# Revit family: Haworth_9_OccasionalTable
name_source: partatom
category: Furniture
revit_build: Autodesk Revit 2018 (Build: 20170223_1515(x64)
units: mm (PartAtom-declared; Revit-internal decimal feet)

## family parameters
Always vertical = Yes
Cut with Voids When Loaded = No
OmniClass Number = 23.40.70.14.64.21
OmniClass Title = Systems Furniture
Room Calculation Point = No
Shared = No
Work Plane-Based = No

## types (10) — shared parameters
Assembly Code = E2020200
Description = Haworth - Cassina - 9 - Occasional Table
Manufacturer = Haworth
Model = Haworth - Cassina - 9
Revision Number = 1
Size = Verify Final Dim. w/ Haworth
Sustainability Info = https://www.haworth.com
URL = https://www.haworth.com
URL - Product = https://www.haworth.com
Warranty = http://www.haworth.com

## per-type parameters (varying)
| type | Actual Depth | Actual Diameter | Actual Height | Bottom Base | Glass Top | Height Diff for Stone Top | High | Large | Low | Medium | Small | Wood or Stone Top |
| Low Occasional Table -  Glass Top With Stone Base | 15.7 " | 15.7 " | 17.7 " | 3.92 " | Yes | 0 " | No | No | Yes | No | Yes | No |
| Medium Occasional Table -  Glass Top With Stone Base | 15.7 " | 15.7 " | 19.7 " | 3.92 " | Yes | 0 " | No | No | No | Yes | Yes | No |
| High Occasional Table -  Glass Top With Stone Base | 15.7 " | 15.7 " | 21.7 " | 3.92 " | Yes | 0 " | Yes | No | No | No | Yes | No |
| Low Occasional Table -  Wood Top And Base | 15.7 " | 15.7 " | 17.3 " | 3.92 " | No | 0.4 " | No | No | Yes | No | Yes | Yes |
| Medium Occasional Table -  Wood Top And Base | 15.7 " | 15.7 " | 19.3 " | 3.92 " | No | 0.4 " | No | No | No | Yes | Yes | Yes |
| High Occasional Table -  Wood Top And Base | 15.7 " | 15.7 " | 21.3 " | 3.92 " | No | 0.4 " | Yes | No | No | No | Yes | Yes |
| Low Occasional Table -  Stone Top And Base | 15.7 " | 15.7 " | 17.3 " | 3.92 " | No | 0.4 " | No | No | Yes | No | Yes | Yes |
| Medium Occasional Table -  Stone Top And Base | 15.7 " | 15.7 " | 19.3 " | 3.92 " | No | 0.4 " | No | No | No | Yes | Yes | Yes |
| High Occasional Table -  Stone Top And Base | 15.7 " | 15.7 " | 21.3 " | 3.92 " | No | 0.4 " | Yes | No | No | No | Yes | Yes |
| Large Occasional Table -  Glass Top With Stone Base | 27.6 " | 27.6 " | 11.1 " | 9.74 " | Yes | 0 " | Yes | Yes | No | No | No | No |

## geometry (parser evidence)
native form markers: Sweep x9
no freeform markers — native parametric forms only
